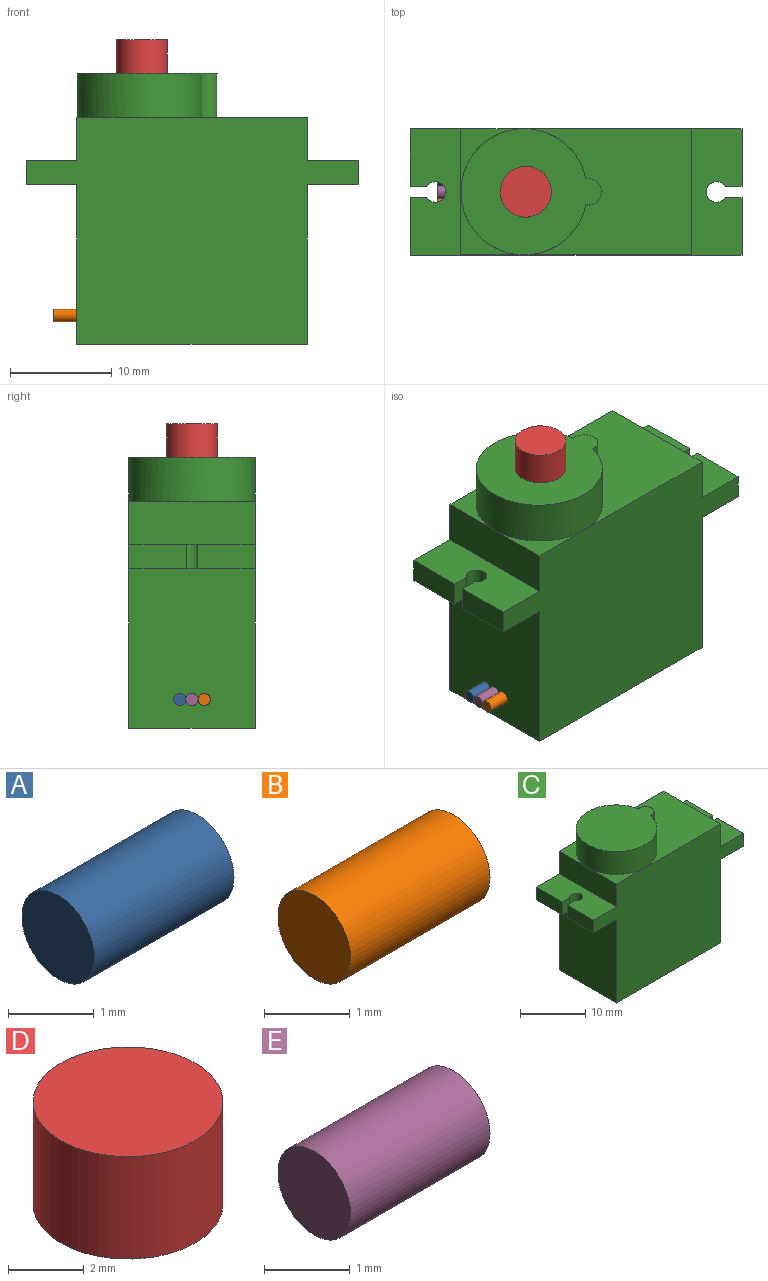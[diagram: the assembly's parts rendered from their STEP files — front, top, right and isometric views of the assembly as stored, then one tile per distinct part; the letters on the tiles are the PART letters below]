
ASSEMBLY  parts=5 mates=4
PART A: 3 faces, bbox 2.3x1.2x1.2 mm
  f0: cylinder r=0.6mm len=2.3mm, axis (1,0,0), area 8.7mm2, adj f1,f2
  f1: plane 1.2x1.2mm, normal (-1,0,0), area 1.1mm2, adj f0
  f2: plane 1.2x1.2mm, normal (1,0,0), area 1.1mm2, adj f0
PART B: 3 faces, bbox 2.3x1.2x1.2 mm
  f0: cylinder r=0.6mm len=2.3mm, axis (1,0,0), area 8.7mm2, adj f1,f2
  f1: plane 1.2x1.2mm, normal (-1,0,0), area 1.1mm2, adj f0
  f2: plane 1.2x1.2mm, normal (1,0,0), area 1.1mm2, adj f0
PART C: 27 faces, bbox 32.6x12.4x26.6 mm
  f0: plane 12.4x4.25mm, normal (-1,0,0), area 52.7mm2, adj f7,f8,f9,f10,f22
  f1: plane 15.65x12.4mm, normal (-1,0,0), area 194.1mm2, adj f8,f9,f11,f23
  f2: plane 12.4x4.25mm, normal (1,0,0), area 52.7mm2, adj f6,f8,f9,f15
  f3: plane 15.65x12.4mm, normal (1,0,0), area 194.1mm2, adj f8,f9,f11,f14
  f4: cylinder r=6.2mm len=12.4mm, axis (0,0,-1), area 156.4mm2, adj f5,f6,f7,f10,f12
  f5: cylinder r=1.3mm len=4.3mm, axis (0,0,-1), area 19.6mm2, adj f4,f6,f12
  f6: plane 16.4x12.4mm, normal (0,0,1), area 139.9mm2, adj f2,f4,f5,f8,f9
  f7: plane 6.2x6.2mm, normal (0,0,1), area 8.2mm2, adj f0,f4,f8
  f8: plane 32.6x22.3mm, normal (0,1,0), area 528mm2, adj f0,f1,f2,f3,f6,f7,f11,f14
  f9: plane 32.6x22.3mm, normal (0,-1,0), area 528mm2, adj f0,f1,f2,f3,f6,f10,f11,f14
  f10: plane 6.2x6.2mm, normal (0,0,1), area 8.2mm2, adj f0,f4,f9
  f11: plane 22.6x12.4mm, normal (0,0,-1), area 280.2mm2, adj f1,f3,f8,f9
  f12: plane 13.8x12.4mm, normal (0,0,1), area 123.8mm2, adj f4,f5
  f13: cylinder r=1mm len=2.4mm, axis (0,0,1), area 12.3mm2, adj f14,f15,f18,f19
  f14: plane 12.4x5mm, normal (0,0,-1), area 57.2mm2, adj f3,f8,f9,f13,f16,f17,f18,f19
  f15: plane 12.4x5mm, normal (0,0,1), area 57.2mm2, adj f2,f8,f9,f13,f16,f17,f18,f19
  f16: plane 5.65x2.4mm, normal (1,0,0), area 13.6mm2, adj f8,f14,f15,f18
  f17: plane 5.65x2.4mm, normal (1,0,0), area 13.6mm2, adj f9,f14,f15,f19
  f18: plane 2.4x1.67mm, normal (0,-1,0), area 4mm2, adj f13,f14,f15,f16
  f19: plane 2.4x1.67mm, normal (0,1,0), area 4mm2, adj f13,f14,f15,f17
  f20: cylinder r=1mm len=2.4mm, axis (0,0,1), area 12.3mm2, adj f22,f23,f25,f26
  f21: plane 5.65x2.4mm, normal (-1,0,0), area 13.6mm2, adj f8,f22,f23,f25
  f22: plane 12.4x5mm, normal (0,0,1), area 57.2mm2, adj f0,f8,f9,f20,f21,f24,f25,f26
  f23: plane 12.4x5mm, normal (0,0,-1), area 57.2mm2, adj f1,f8,f9,f20,f21,f24,f25,f26
  f24: plane 5.65x2.4mm, normal (-1,0,0), area 13.6mm2, adj f9,f22,f23,f26
  f25: plane 2.4x1.67mm, normal (0,-1,0), area 4mm2, adj f20,f21,f22,f23
  f26: plane 2.4x1.67mm, normal (0,1,0), area 4mm2, adj f20,f22,f23,f24
PART D: 3 faces, bbox 5x5x3.3 mm
  f0: plane 5x5mm, normal (0,0,1), area 19.6mm2, adj f1
  f1: cylinder r=2.5mm len=5mm, axis (0,0,-1), area 51.8mm2, adj f0,f2
  f2: plane 5x5mm, normal (0,0,-1), area 19.6mm2, adj f1
PART E: 3 faces, bbox 2.3x1.2x1.2 mm
  f0: cylinder r=0.6mm len=2.3mm, axis (1,0,0), area 8.7mm2, adj f1,f2
  f1: plane 1.2x1.2mm, normal (-1,0,0), area 1.1mm2, adj f0
  f2: plane 1.2x1.2mm, normal (1,0,0), area 1.1mm2, adj f0
PLACE A t=(0,0,-1.68)mm
PLACE B t=(0,0,-1.68)mm
PLACE C at identity
PLACE D t=(0.17,0,0)mm
PLACE E t=(0,0,-1.68)mm
MATE revolute D.f1 <-> C.f12  axis (0,0,-1) through (-4.93,0,26.6)mm
MATE fastened A.f0 <-> C.f1  axis (1,0,0) through (-11.3,1.2,2.83)mm
MATE fastened B.f0 <-> C.f1  axis (1,0,0) through (-11.3,-1.2,2.83)mm
MATE fastened E.f0 <-> C.f1  axis (1,0,0) through (-11.3,0,2.83)mm
